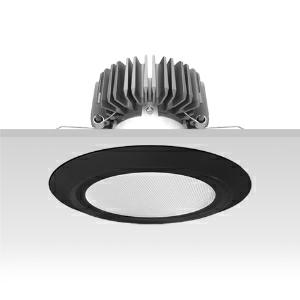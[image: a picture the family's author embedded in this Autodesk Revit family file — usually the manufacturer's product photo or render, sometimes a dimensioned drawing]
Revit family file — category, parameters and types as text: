
# Revit family: 3f_filippi_-_3f_reno_bianco_ampio_3f_filippi_-_30671_a01038_-_3f_reno_200_wh_2000-840_dali_wide___vs_bk_c1a8
name_source: partatom
category: Lighting Fixtures
units: mm (PartAtom-declared; Revit-internal decimal feet)

## family parameters
Cut with Voids When Loaded = No
Host = Face
Light Source = No
Part Type = Normal
Room Calculation Point = No
Round Connector Dimension = Use Diameter
Shared = No

## types (1)
- 3F Filippi - 3F Reno Bianco Ampio (1 x LED, 1723 lm, 20 W, 4000 K)
    Apparent Load = 20 VA
    Approval mark = CE
    CIE Flux Codes = 75 94 99 100 100
    Color Rendering = 80
    Color Temperature = 4000 K
    Control Gear = Electronic transformer
    Default Elevation = 1800 mm
    Description = ILLUMINOTECHNICAL
Luminous efficiency 100% (DLOR 100%, ULOR 0%).
Initial luminous flux of the luminaire 1723 lm.
Direct symmetric wide distribution.
Installation Interdistance Transv.D = 1.16 x hu - Long.D = 1.14 x hu.
Average luminance <3000 cd/m² for radial angles >65°.
Tabular UGR (CIE 117 - 4H-8H; S=0.25H; 70/50/20): RUG 20.4 - 20.3.
Beam angle: 74° - 74°.
Luminous efficacy 86 lm/W.
Lifetime (L90/B10): 30000 h. (tq+25°C)
Lifetime (L85/B10): 50000 h. (tq+25°C)
Lifetime (L70/B10): 80000 h. (tq+25°C)
Sudden decreased luminous flux after 50000 hours: 0% (C0).
Photobiological safety in compliance with IEC/TR 62778: RG0 risk exempt, (IEC 62471).
In compliance with IEC/EN 62722-2-1 - IEC/EN 62717 standards.

SOURCE
Compact LED module 2000/840.
Energy efficiency class (UE 2019/2020 - UE 2019/2015): D.
CIE 13.3 Colour rendering index: CRI >80 (R9 <50%).
IES TM-30 Fidelity Index: Rf = 84 Rg = 95.
CCT nominal colour temperature 4000 K.
Colour initial tolerance (MacAdam): SDCM 3.
Zhaga Book 3 compliant.

MECHANICAL
Passive heat dissipator in die-casting aluminium, oversized, for optimum thermal management of the LED module.
Parabolic element with graduated/concentric rings in white polycarbonate.
Transparent external lens with glossy and satin differentiated surfaces, with a cooling and anti-insect system in methacrylate (PMMA).
Fastening spring clips in stainless steel.
Dimensions: diameter 226 mm, height 146 mm. Weight 1.23 kg.
IP44 protection degree for exposed part, IP20 for recessed part.
Mechanical strength to impacts IK06 (1 joule).
Glow-wire test resistance 650°C.

ELECTRICAL
Wiring on a separate unit.
Halogen Free DALI-2 DATI (Parts 251, 252, 253), PUSH-DIM, electronic wiring 230V-50/60Hz, power factor 0.90 at full load, THD <25%, constant output current, SELV, class II, 1 driver, 1 DALI addresse.
Power of the luminaire 20 W.
ENEC - CE.
SAFE FLICKER: PstLM=<1 and SVM=<0.4 (IEC TR 61547-1 and IEC TR 63158), to ensure a more comfortable and safe light.
Luminaire compliant with EN 60598-2-22 for power supply from a centralised emergency system CPSS (Central Power Supply System), not incorporated in the luminaire - high risk areas excluded. The default power and flux are 100% in AC and 100% in DC.
Ambient temperature from 0°C to +25°C.
Temperature class T6 max 85°C.
Relative humidity UR: <85%.

INSTALLATION
Pull-up recessed fitting.
False ceiling carving: 200 mm.
All accessories dedicated to this product are available on the Catalog and on our website www.3F-Filippi.com.

ACCESSORIES
A01038 - Anti-glare microprismatic VS moulded glass, tempered, not flammable, locked and in line with the trim, in black polycarbonate.

APPLICATIONS
Environments: architectural, commercial, exhibition areas, transit areas, corridors, shops, display windows, service areas.
In false ceilings with narrow voids.

LIGHT MANAGEMENT
Recommended minimum setting: 10%.
The luminaire, equipped with (DALI-2 DATI) driver, can be controlled manually with 3F Easy Dim technology or automatically/manually with wired or wireless DALI/D2D control systems.
The D2D driver guarantees interoperability with other devices with the same certification by making the following information available:
Device Data (Part 251), Energy Report (Part 252), Diagnosis & Maintenance (Part 253).
In electrical systems without a regulation system (manual or automatic) and DALI bus, a suitable jumper must be made on the DA-DA terminals of the appliance.

WARNING
Luminaire designed for disposal/recycling at end-of-life.
Replaceable (LED only) light source by a professional. Replaceable control gear by a professional.
    Height = 0 mm  [stored 0 ft]
    Lamp = 1 x LED
    Lamp Light Flux = 1723 lm
    Lamp Power = 20 W
    Lamp count = 1
    Length = 226 mm
    Lifetime = 50000 h
    Luminous efficacy = 86 lm/W
    Manufacturer = 3F Filippi
    ModVariant = No
    Model = 3F Filippi - 30671+A01038 - 3F Reno 200 WH 2000-840 DALI WIDE + VS BK
    Mounting Place = Ceiling
    Mounting Type = Recessed
    Number of Poles = 1
    OnlyDefault = Yes
    Power Factor = 1
    Product Name = 3F Filippi - 3F Reno Bianco Ampio
    Product group = recessed luminaire
    ProductGroupID = 4
    Protection Class = Protection class II
    Protection Degree = IP 20
    RLX_Detail_Level = 1
    RLX_Emergency_Light_Flux = 0 lm
    RLX_Emergency_Type = 0
    RLX_Emergency_Type_DB = No
    RlxData = <blob elided: 99437 chars, md5=58e2189e>
    Socket = socket
    Standby Power = 0 W
    System Light Flux = 1723 lm
    System Power = 20 W
    Type Comments = Product without accessories
    Type Image = 3ffilippi_3f_reno_200_bk_vs_smp.jpg
    URL = http://relux.com
    VarID = ---
    Voltage = 0 V
    Weight = 0.00 kg
    Width = 0 mm  [stored 0 ft]

note: [stored X ft] marks values corroborated as IEEE doubles in the binary element streams (Revit-internal decimal feet)

## geometry (parser evidence)
native form markers: Blend x4, Sweep x10
no freeform markers — native parametric forms only
